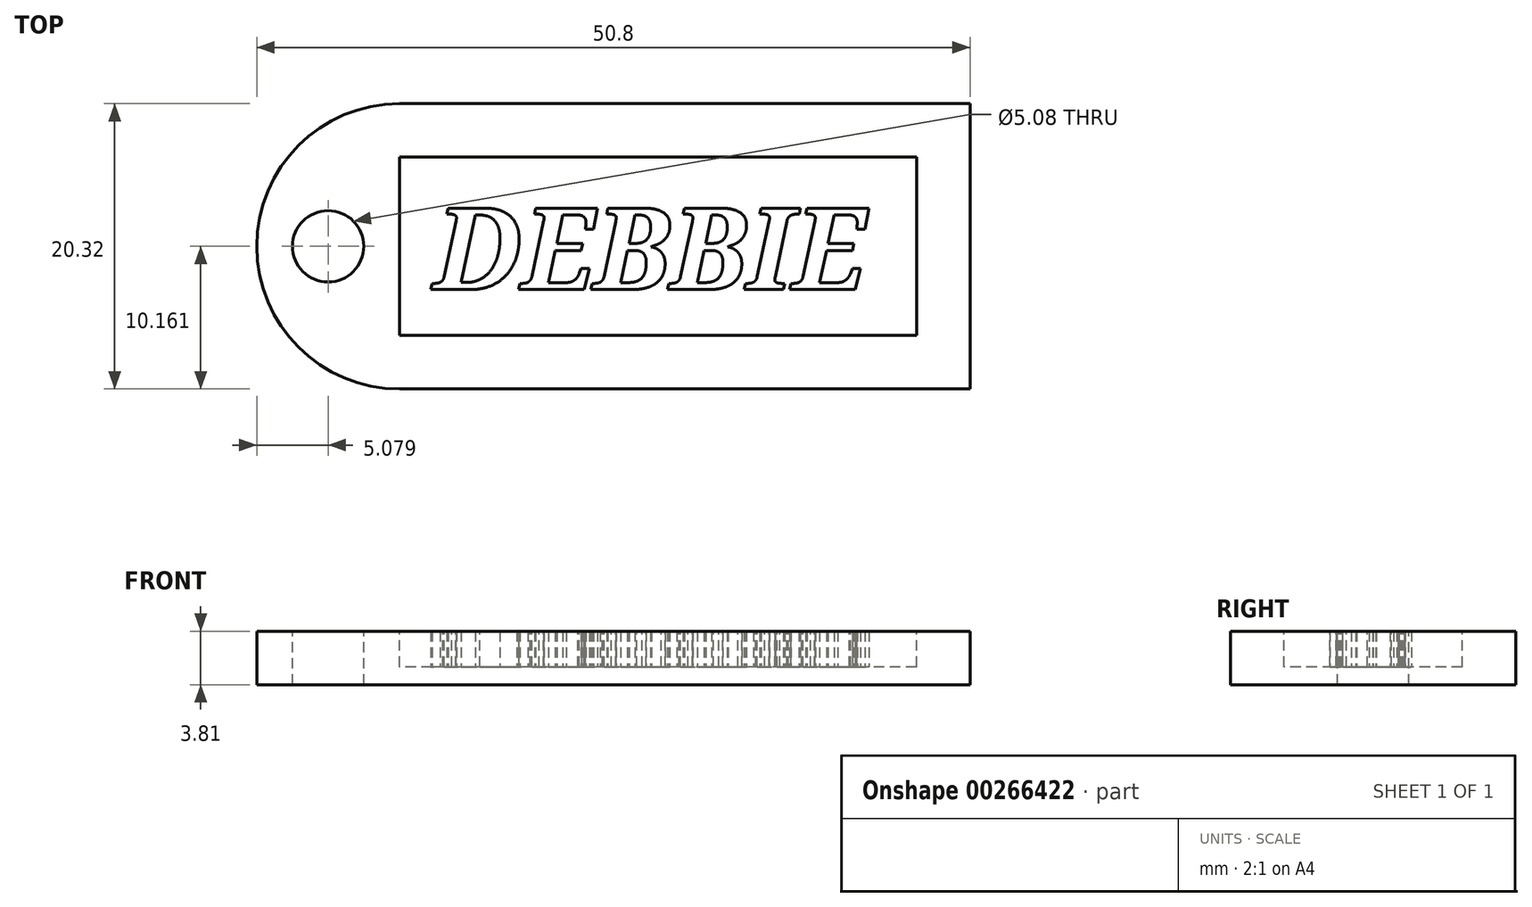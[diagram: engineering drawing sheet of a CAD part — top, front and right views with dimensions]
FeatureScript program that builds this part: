
annotation { "Feature Type Name" : "Feature", "Feature Type Description" : "" }
export const myFeature = defineFeature(function(context is Context, id is Id, definition is map)
    precondition{}
    {
        {
            var Q0;
            Q0=qCreatedBy(makeId("Top.planeOp"),FACE);
            var sketch = newSketch(context, id + "F0", { "sketchPlane" : qUnion([Q0])});
            skLineSegment(sketch, "E0.bottom", {"start": v(-8.05, 40.52) * mm, "end": v(32.59, 40.52) * mm});
            skLineSegment(sketch, "E0.top", {"start": v(-8.05, 20.2) * mm, "end": v(32.59, 20.2) * mm});
            skLineSegment(sketch, "E0.left", {"start": v(-18.21, 30.36) * mm, "end": v(-18.21, 30.36) * mm});
            skLineSegment(sketch, "E0.right", {"start": v(32.59, 40.52) * mm, "end": v(32.59, 20.2) * mm});
            skPoint(sketch, "E1.visualSharp", {"position": v(-18.21, 40.52) * mm});
            skArc(sketch, "E1.filletArc", {"start": v(-8.05, 40.52) * mm, "mid": v(-15.24, 37.54) * mm, "end": v(-18.21, 30.36) * mm});
            skPoint(sketch, "E2.visualSharp", {"position": v(-18.21, 20.2) * mm});
            skArc(sketch, "E2.filletArc", {"start": v(-18.21, 30.36) * mm, "mid": v(-15.24, 23.18) * mm, "end": v(-8.05, 20.2) * mm});
            skSolve(sketch);
        }
        {
            var Q0;
            Q0 = qSketchRegion(id + "F0", true);
            extrude(context, id + "F1", {"entities" : qUnion([Q0]), "depth" : 3.8 * mm});
        }
        {
            var Q0;
            Q0=makeQuery(id+"F1.opExtrude","CAP_FACE",FACE,{"disambiguationData":[OSD([sQuery(id+"F0.wireOp",EDGE,"E0.bottom"),sQuery(id+"F0.wireOp",EDGE,"E0.top"),sQuery(id+"F0.wireOp",EDGE,"E0.right"),sQuery(id+"F0.wireOp",EDGE,"E1.filletArc"),sQuery(id+"F0.wireOp",EDGE,"E2.filletArc")])],"isStart":false});
            var sketch = newSketch(context, id + "F2", { "sketchPlane" : qUnion([Q0])});
            skPoint(sketch, "E3", {"position": v(28.78, 36.71) * mm});
            skPoint(sketch, "E4", {"position": v(103.23, -37.27) * mm});
            skPoint(sketch, "E5", {"position": v(-8.05, 24.01) * mm});
            skLineSegment(sketch, "E6.bottom", {"start": v(28.78, 36.71) * mm, "end": v(-8.05, 36.71) * mm});
            skLineSegment(sketch, "E6.top", {"start": v(28.78, 24.01) * mm, "end": v(-8.05, 24.01) * mm});
            skLineSegment(sketch, "E6.left", {"start": v(28.78, 36.71) * mm, "end": v(28.78, 24.01) * mm});
            skLineSegment(sketch, "E6.right", {"start": v(-8.05, 36.71) * mm, "end": v(-8.05, 24.01) * mm});
            skSolve(sketch);
        }
        {
            var Q0;
            Q0 = qSketchRegion(id + "F2", true);
            extrude(context, id + "F3", {"entities" : qUnion([Q0]), "operationType" : NewBodyOperationType.REMOVE, "oppositeDirection" : true, "depth" : 2.54 * mm});
        }
        {
            var Q0;
            Q0=makeQuery(id+"F1.opExtrude","CAP_FACE",FACE,{"disambiguationData":[OSD([sQuery(id+"F0.wireOp",EDGE,"E0.bottom"),sQuery(id+"F0.wireOp",EDGE,"E0.top"),sQuery(id+"F0.wireOp",EDGE,"E0.right"),sQuery(id+"F0.wireOp",EDGE,"E1.filletArc"),sQuery(id+"F0.wireOp",EDGE,"E2.filletArc")])],"isStart":false});
            var sketch = newSketch(context, id + "F4", { "sketchPlane" : qUnion([Q0])});
            skPoint(sketch, "E7", {"position": v(-13.13, 30.36) * mm});
            skPoint(sketch, "E7.positionSnap0", {"position": v(-18.21, 30.36) * mm});
            skCircle(sketch, "E8", {"center": v(-13.13, 30.36) * mm, "radius": 2.54 * mm});
            skSolve(sketch);
        }
        {
            var Q0;
            Q0 = qSketchRegion(id + "F4", true);
            extrude(context, id + "F5", {"entities" : qUnion([Q0]), "operationType" : NewBodyOperationType.REMOVE, "oppositeDirection" : true, "depth" : 25.4 * mm});
        }
        {
            var Q0;
            Q0=makeQuery(id+"F3.boolean.opBoolean","COPY",FACE,{"derivedFrom":makeQuery(id+"F3.opExtrude","CAP_FACE",FACE,{"disambiguationData":[OSD([sQuery(id+"F2.wireOp",EDGE,"E6.bottom"),sQuery(id+"F2.wireOp",EDGE,"E6.top"),sQuery(id+"F2.wireOp",EDGE,"E6.left"),sQuery(id+"F2.wireOp",EDGE,"E6.right")])],"isStart":false})});
            var sketch = newSketch(context, id + "F6", { "sketchPlane" : qUnion([Q0])});
            skText(sketch, "E9", { "text": "DEBBIE", "fontName": "NotoSerif-BoldItalic.ttf"});
            const initialGuessF6  = {"E9": [-0.00562, 0.02728, 1, 0, 0.00585]};
            skSetInitialGuess(sketch, initialGuessF6);
            skSolve(sketch);
        }
        {
            var Q0;
            Q0 = qSketchRegion(id + "F6", true);
            extrude(context, id + "F7", {"entities" : qUnion([Q0]), "operationType" : NewBodyOperationType.ADD, "depth" : 2.54 * mm});
        }
    });
